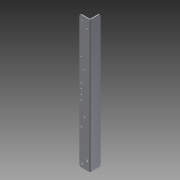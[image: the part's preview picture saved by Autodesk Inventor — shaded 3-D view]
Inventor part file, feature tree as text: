
AUTODESK INVENTOR PART (.ipt)
format: ipt  version: 2014 SP1 (Build 180222100, 222)  size: 261,632 bytes
history: native  units: in
note: dims shown in document units (in); Inventor stores cm internally (conversion verified against a paired STEP export)
features: other x5, sketch x4, sheet_metal_op x2, reference x2, chamfer x1
ambient origin geometry x8: Origin, YZ Plane, XZ Plane, XY Plane, X Axis, Y Axis, Z Axis, Center Point
bodies: Solid1 (feature_tree)
feature tree (14):
  sketch  "Sketch1"  dims[d0=20.0in]
  sheet_metal_op  "Face1"
  sheet_metal_op  "Fold1"
  chamfer  "Corner Round1"
  other  "Plate1"
  sketch  "Sketch2"  dims[d1=3.0in]
  sketch  "Sketch3"  dims[d2=1.5in]
  reference  "Reference1"
  reference  "Reference2"
  sketch  "Sketch4"  dims[d3=0.25in d4=0.01in d5=0.25in d6=11.811in d8=0.6638in d9=0.3937in d11=1.0in d13=0.125in d14=0.125in d15=0.0625in d16=0.25in d17=0.125in d18=90.0deg d19=0.05in d20=0.313in d22=0.75in d23=0.313in d24=0.313in d25=0.375in d26=0.75in d27=0.75in d28=0.55in d29=0.125in d30=0.0in d31=6.2008in d32=0.266in d34=0.266in d36=1.5748in d38=0.75in d39=0.3937in d41=1.0in d43=0.25in d44=0.125in d45=0.0in d46=0.25in d47=0.875in d48=0.875in d49=1.5in d50=4.7244in d52=1.5455in d53=0.3937in d55=1.0in d57=0.266in d58=0.266in d59=0.25in d60=9.25in d61=0.125in d62=0.0in]
  other  "Cut1"
  other  "Cut2"
  other  "Cut3"
  other  "Definition1"
